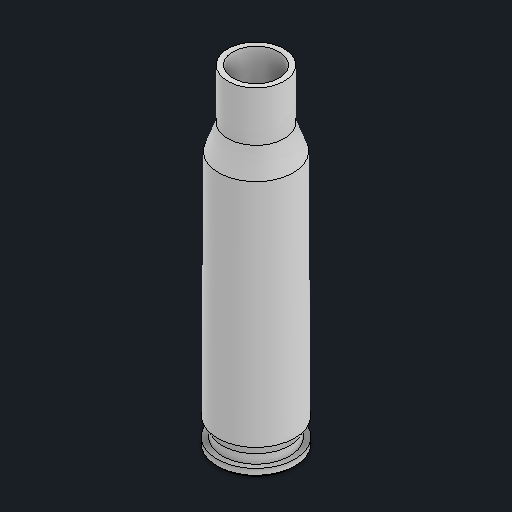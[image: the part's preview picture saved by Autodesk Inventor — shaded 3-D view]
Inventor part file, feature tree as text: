
AUTODESK INVENTOR PART (.ipt)
format: ipt  version: 2025.1 (Build 291241020, 241B)  size: 152,064 bytes
history: native  units: in
note: dims shown in document units (in); Inventor stores cm internally (conversion verified against a paired STEP export)
features: sketch x7, plane x6, loft x4, other x4, extrude x2, chamfer x1, shell x1
ambient origin geometry x8: Origin, YZ Plane, XZ Plane, XY Plane, X Axis, Y Axis, Z Axis, Center Point
bodies: Solid1 (feature_tree)
feature tree (25):
  sketch  "Sketch1"  dims[d0=0.473in]
  plane  "Work Plane1"
  plane  "Work Plane2"
  plane  "Work Plane3"
  plane  "Work Plane4"
  plane  "Work Plane5"
  plane  "Work Plane7"
  sketch  "Sketch2"  dims[d1=0.054in d2=0.055in d3=1.56in d4=1.712in d5=2.015in d6=0.409in]
  sketch  "Sketch3"  dims[d7=0.409in d8=0.454in]
  sketch  "Sketch4"  dims[d9=0.343in d10=0.343in]
  sketch  "Sketch5"  dims[d11=1.0in d12=0.0in d13=1.0in d14=0.0in]
  sketch  "Sketch6"  dims[d27=0.018in d28=0.125in d29=45.0deg d36=0.055in]
  sketch  "Sketch8"  dims[d37=0.47in d38=0.0in d39=90.0deg d40=0.0in d41=90.0deg d42=0.0in d43=90.0deg d44=0.0in d45=90.0deg d46=0.0in d47=90.0deg d48=0.0in d49=90.0deg d50=0.0in d51=90.0deg d52=0.0in d53=90.0deg d54=0.0315in]
  extrude  "Extrusion1"  Depth=2.015in
  extrude  "Extrusion2"  Depth=0.454in
  loft  "Loft5"
  loft  "Loft6"
  loft  "Loft7"
  loft  "Loft8"
  chamfer  "Chamfer1"  Angle=90.0deg  [1 undecoded]
  shell  "Shell1"  Thickness=0.0in
  other  "Edges4"
  other  "Edges5"
  other  "Edges6"
  other  "Edges7"
note: 1 required parameter value undecoded (feature->parameter linkage not recoverable at this tier; creation-order binding heuristic only, values carry confidence <= 0.55)
